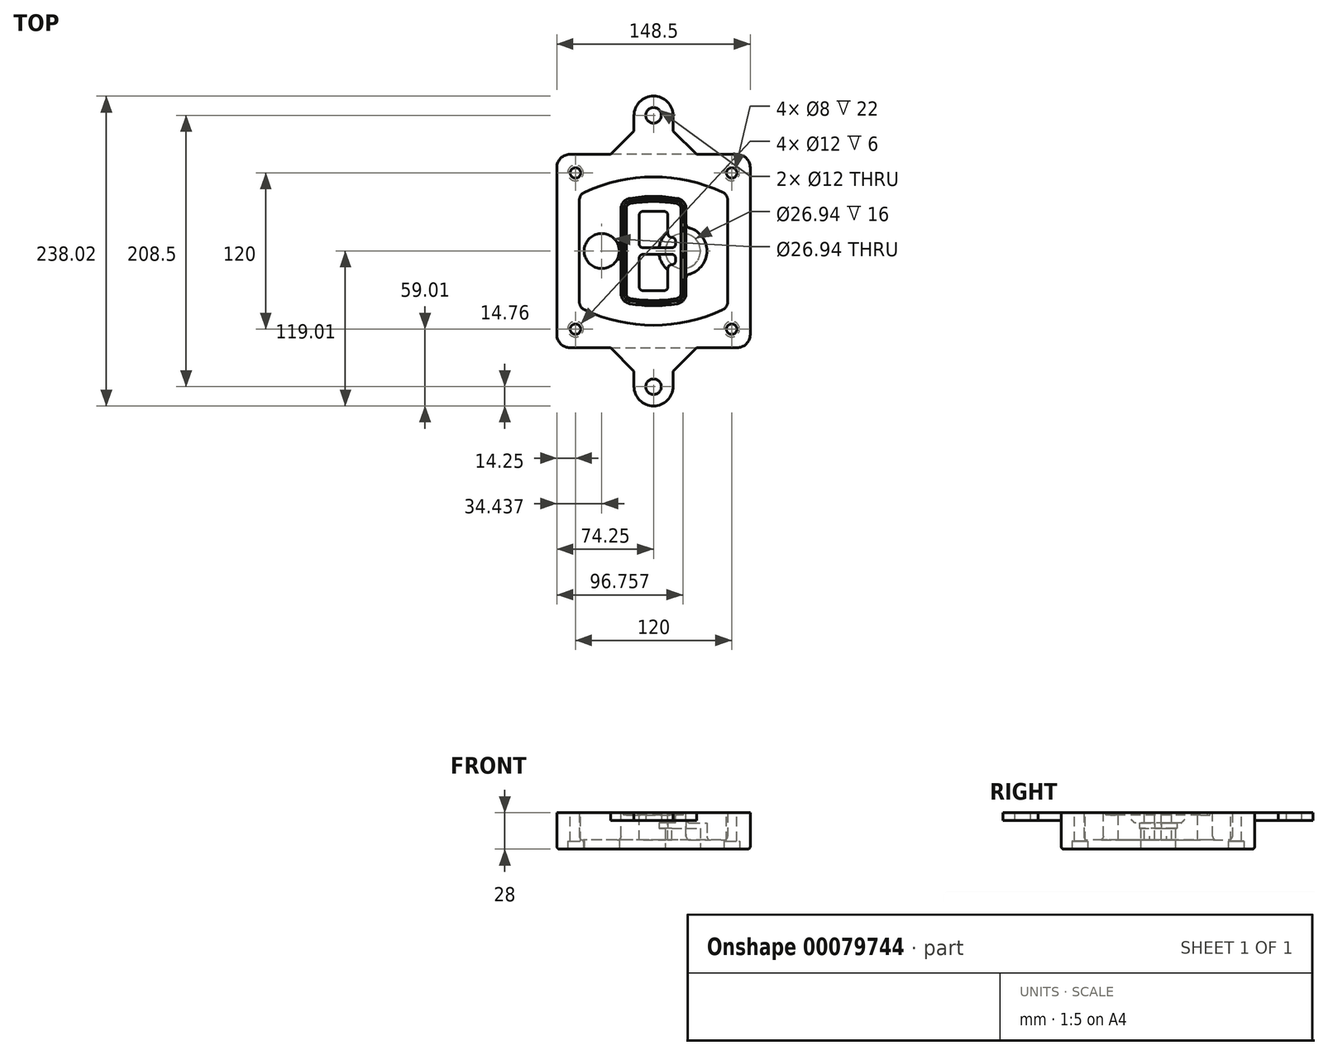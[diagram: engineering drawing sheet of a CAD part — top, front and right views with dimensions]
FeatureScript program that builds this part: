
annotation { "Feature Type Name" : "Feature", "Feature Type Description" : "" }
export const myFeature = defineFeature(function(context is Context, id is Id, definition is map)
    precondition{}
    {
        {
            var Q0;
            Q0=qCreatedBy(makeId("Top.planeOp"),FACE);
            var sketch = newSketch(context, id + "F0", { "sketchPlane" : qUnion([Q0])});
            skPoint(sketch, "E0.rect.middle", {"position": v(0, 0) * mm});
            skLineSegment(sketch, "E1.bottom", {"start": v(-64.25, -74.25) * mm, "end": v(64.25, -74.25) * mm});
            skLineSegment(sketch, "E1.top", {"start": v(-64.25, 74.25) * mm, "end": v(64.25, 74.25) * mm});
            skLineSegment(sketch, "E1.left", {"start": v(-74.25, -64.25) * mm, "end": v(-74.25, 64.25) * mm});
            skLineSegment(sketch, "E1.right", {"start": v(74.25, -64.25) * mm, "end": v(74.25, 64.25) * mm});
            skLineSegment(sketch, "E2", {"start": v(-74.25, 74.25) * mm, "end": v(74.25, -74.25) * mm, "construction": true});
            skLineSegment(sketch, "E3", {"start": v(74.25, 74.25) * mm, "end": v(-74.25, -74.25) * mm, "construction": true});
            skCircle(sketch, "E4", {"center": v(-60, 60) * mm, "radius": 4 * mm});
            skCircle(sketch, "E5", {"center": v(60, 60) * mm, "radius": 4 * mm});
            skCircle(sketch, "E6", {"center": v(60, -60) * mm, "radius": 4 * mm});
            skCircle(sketch, "E7", {"center": v(-60, -60) * mm, "radius": 4 * mm});
            skLineSegment(sketch, "E8", {"start": v(-60, 60) * mm, "end": v(60, 60) * mm, "construction": true});
            skLineSegment(sketch, "E9", {"start": v(60, 60) * mm, "end": v(60, -60) * mm, "construction": true});
            skLineSegment(sketch, "E10", {"start": v(60, -60) * mm, "end": v(-60, -60) * mm, "construction": true});
            skLineSegment(sketch, "E11", {"start": v(-60, -60) * mm, "end": v(-60, 60) * mm, "construction": true});
            skLineSegment(sketch, "E12", {"start": v(-60, 38.83) * mm, "end": v(-60, -38.83) * mm});
            skLineSegment(sketch, "E13", {"start": v(60, 38.83) * mm, "end": v(60, -38.83) * mm});
            skArc(sketch, "E14", {"start": v(54.26, 47.88) * mm, "mid": v(0, 60) * mm, "end": v(-54.26, 47.88) * mm});
            skArc(sketch, "E15", {"start": v(-54.26, -47.88) * mm, "mid": v(0, -60) * mm, "end": v(54.26, -47.88) * mm});
            skLineSegment(sketch, "E16", {"start": v(-60, 0) * mm, "end": v(60, 0) * mm, "construction": true});
            skPoint(sketch, "E17.visualSharp", {"position": v(-60, -45) * mm});
            skArc(sketch, "E17.filletArc", {"start": v(-60, -38.83) * mm, "mid": v(-58.44, -44.2) * mm, "end": v(-54.26, -47.88) * mm});
            skPoint(sketch, "E18.visualSharp", {"position": v(-60, 45) * mm});
            skArc(sketch, "E18.filletArc", {"start": v(-54.26, 47.88) * mm, "mid": v(-58.44, 44.2) * mm, "end": v(-60, 38.83) * mm});
            skPoint(sketch, "E19.visualSharp", {"position": v(60, 45) * mm});
            skArc(sketch, "E19.filletArc", {"start": v(60, 38.83) * mm, "mid": v(58.44, 44.2) * mm, "end": v(54.26, 47.88) * mm});
            skPoint(sketch, "E20.visualSharp", {"position": v(60, -45) * mm});
            skArc(sketch, "E20.filletArc", {"start": v(54.26, -47.88) * mm, "mid": v(58.44, -44.2) * mm, "end": v(60, -38.83) * mm});
            skPoint(sketch, "E21.visualSharp", {"position": v(-74.25, 74.25) * mm});
            skArc(sketch, "E21.filletArc", {"start": v(-64.25, 74.25) * mm, "mid": v(-71.32, 71.32) * mm, "end": v(-74.25, 64.25) * mm});
            skPoint(sketch, "E22.visualSharp", {"position": v(74.25, 74.25) * mm});
            skArc(sketch, "E22.filletArc", {"start": v(74.25, 64.25) * mm, "mid": v(71.32, 71.32) * mm, "end": v(64.25, 74.25) * mm});
            skPoint(sketch, "E23.visualSharp", {"position": v(74.25, -74.25) * mm});
            skArc(sketch, "E23.filletArc", {"start": v(64.25, -74.25) * mm, "mid": v(71.32, -71.32) * mm, "end": v(74.25, -64.25) * mm});
            skPoint(sketch, "E24.visualSharp", {"position": v(-74.25, -74.25) * mm});
            skArc(sketch, "E24.filletArc", {"start": v(-74.25, -64.25) * mm, "mid": v(-71.32, -71.32) * mm, "end": v(-64.25, -74.25) * mm});
            skArc(sketch, "E25.0", {"start": v(57, 38.83) * mm, "mid": v(55.9, 42.58) * mm, "end": v(52.98, 45.17) * mm});
            skLineSegment(sketch, "E25.1", {"start": v(57, 38.83) * mm, "end": v(57, -38.83) * mm});
            skArc(sketch, "E25.2", {"start": v(52.98, -45.17) * mm, "mid": v(55.9, -42.58) * mm, "end": v(57, -38.83) * mm});
            skArc(sketch, "E25.3", {"start": v(-52.98, -45.17) * mm, "mid": v(0, -57) * mm, "end": v(52.98, -45.17) * mm});
            skArc(sketch, "E25.4", {"start": v(-57, -38.83) * mm, "mid": v(-55.9, -42.58) * mm, "end": v(-52.98, -45.17) * mm});
            skArc(sketch, "E25.5", {"start": v(52.98, 45.17) * mm, "mid": v(0, 57) * mm, "end": v(-52.98, 45.17) * mm});
            skLineSegment(sketch, "E25.6", {"start": v(-57, 38.83) * mm, "end": v(-57, -38.83) * mm});
            skArc(sketch, "E25.7", {"start": v(-52.98, 45.17) * mm, "mid": v(-55.9, 42.58) * mm, "end": v(-57, 38.83) * mm});
            skArc(sketch, "E26.0", {"start": v(-55.96, 51.5) * mm, "mid": v(-61.82, 46.33) * mm, "end": v(-64, 38.83) * mm});
            skArc(sketch, "E26.1", {"start": v(55.96, 51.5) * mm, "mid": v(0, 64) * mm, "end": v(-55.96, 51.5) * mm});
            skArc(sketch, "E26.2", {"start": v(64, 38.83) * mm, "mid": v(61.82, 46.33) * mm, "end": v(55.96, 51.5) * mm});
            skLineSegment(sketch, "E26.3", {"start": v(64, 38.83) * mm, "end": v(64, -38.83) * mm});
            skArc(sketch, "E26.4", {"start": v(55.96, -51.5) * mm, "mid": v(61.82, -46.33) * mm, "end": v(64, -38.83) * mm});
            skLineSegment(sketch, "E26.5", {"start": v(-64, 38.83) * mm, "end": v(-64, -38.83) * mm});
            skArc(sketch, "E26.6", {"start": v(-55.96, -51.5) * mm, "mid": v(0, -64) * mm, "end": v(55.96, -51.5) * mm});
            skArc(sketch, "E26.7", {"start": v(-64, -38.83) * mm, "mid": v(-61.82, -46.33) * mm, "end": v(-55.96, -51.5) * mm});
            skSolve(sketch);
        }
        {
            var Q0;
            Q0=makeQuery(id+"F0.imprint","IMPRINT",FACE,{"disambiguationData":[TD([[makeQuery(id+"F0.imprint","IMPRINT",EDGE,{"derivedFrom":sQuery(id+"F0.wireOp",EDGE,"E1.bottom")}),1.0]])]});
            var Q1;
            Q1=makeQuery(id+"F0.imprint","IMPRINT",FACE,{"disambiguationData":[TD([[makeQuery(id+"F0.imprint","IMPRINT",EDGE,{"derivedFrom":sQuery(id+"F0.wireOp",EDGE,"E12")}),1.0]])]});
            var Q2;
            Q2=makeQuery(id+"F0.imprint","IMPRINT",FACE,{"disambiguationData":[TD([[makeQuery(id+"F0.imprint","IMPRINT",EDGE,{"derivedFrom":sQuery(id+"F0.wireOp",EDGE,"E25.0")}),1.0]])]});
            var Q3;
            Q3=makeQuery(id+"F0.imprint","IMPRINT",FACE,{"disambiguationData":[TD([[makeQuery(id+"F0.imprint","IMPRINT",EDGE,{"derivedFrom":sQuery(id+"F0.wireOp",EDGE,"E12")}),-1.0]])]});
            extrude(context, id + "F1", {"entities" : qUnion([Q0, Q1, Q2, Q3]), "oppositeDirection" : true, "depth" : 25 * mm});
        }
        {
            var Q0;
            Q0=makeQuery(id+"F0.imprint","IMPRINT",FACE,{"disambiguationData":[TD([[makeQuery(id+"F0.imprint","IMPRINT",EDGE,{"derivedFrom":sQuery(id+"F0.wireOp",EDGE,"E12")}),1.0]])]});
            extrude(context, id + "F2", {"entities" : qUnion([Q0]), "operationType" : NewBodyOperationType.ADD, "depth" : 3 * mm});
        }
        {
            var Q0;
            Q0=makeQuery(id+"F0.imprint","IMPRINT",FACE,{"disambiguationData":[TD([[makeQuery(id+"F0.imprint","IMPRINT",EDGE,{"derivedFrom":sQuery(id+"F0.wireOp",EDGE,"E25.0")}),1.0]])]});
            extrude(context, id + "F3", {"entities" : qUnion([Q0]), "operationType" : NewBodyOperationType.REMOVE, "oppositeDirection" : true, "depth" : 18 * mm});
        }
        {
            var Q0;
            Q0=makeQuery(id+"F2.opExtrude","CAP_FACE",FACE,{"disambiguationData":[OSD([sQuery(id+"F0.wireOp",EDGE,"E12"),sQuery(id+"F0.wireOp",EDGE,"E13"),sQuery(id+"F0.wireOp",EDGE,"E14"),sQuery(id+"F0.wireOp",EDGE,"E15"),sQuery(id+"F0.wireOp",EDGE,"E17.filletArc"),sQuery(id+"F0.wireOp",EDGE,"E18.filletArc"),sQuery(id+"F0.wireOp",EDGE,"E19.filletArc"),sQuery(id+"F0.wireOp",EDGE,"E20.filletArc"),sQuery(id+"F0.wireOp",EDGE,"E25.0"),sQuery(id+"F0.wireOp",EDGE,"E25.1"),sQuery(id+"F0.wireOp",EDGE,"E25.2"),sQuery(id+"F0.wireOp",EDGE,"E25.3"),sQuery(id+"F0.wireOp",EDGE,"E25.4"),sQuery(id+"F0.wireOp",EDGE,"E25.5"),sQuery(id+"F0.wireOp",EDGE,"E25.6"),sQuery(id+"F0.wireOp",EDGE,"E25.7")])],"isStart":false});
            var sketch = newSketch(context, id + "F4", { "sketchPlane" : qUnion([Q0])});
            skArc(sketch, "E27.0", {"start": v(-18.34, -40.45) * mm, "mid": v(0, -42) * mm, "end": v(18.34, -40.45) * mm});
            skArc(sketch, "E28.0", {"start": v(18.34, 40.45) * mm, "mid": v(0, 42) * mm, "end": v(-18.34, 40.45) * mm});
            skLineSegment(sketch, "E29", {"start": v(-25, 32.57) * mm, "end": v(-25, -32.57) * mm});
            skLineSegment(sketch, "E30", {"start": v(25, 32.57) * mm, "end": v(25, -32.57) * mm});
            skLineSegment(sketch, "E31", {"start": v(-25, 39.1) * mm, "end": v(25, 39.1) * mm, "construction": true});
            skLineSegment(sketch, "E32", {"start": v(-25, -39.1) * mm, "end": v(25, -39.1) * mm, "construction": true});
            skPoint(sketch, "E33.visualSharp", {"position": v(-25, 39.1) * mm});
            skArc(sketch, "E33.filletArc", {"start": v(-18.34, 40.45) * mm, "mid": v(-23.11, 37.73) * mm, "end": v(-25, 32.57) * mm});
            skPoint(sketch, "E34.visualSharp", {"position": v(25, 39.1) * mm});
            skArc(sketch, "E34.filletArc", {"start": v(25, 32.57) * mm, "mid": v(23.11, 37.73) * mm, "end": v(18.34, 40.45) * mm});
            skPoint(sketch, "E35.visualSharp", {"position": v(25, -39.1) * mm});
            skArc(sketch, "E35.filletArc", {"start": v(18.34, -40.45) * mm, "mid": v(23.11, -37.73) * mm, "end": v(25, -32.57) * mm});
            skPoint(sketch, "E36.visualSharp", {"position": v(-25, -39.1) * mm});
            skArc(sketch, "E36.filletArc", {"start": v(-25, -32.57) * mm, "mid": v(-23.11, -37.73) * mm, "end": v(-18.34, -40.45) * mm});
            skArc(sketch, "E37.0", {"start": v(52.98, 45.17) * mm, "mid": v(0, 57) * mm, "end": v(-52.98, 45.17) * mm});
            skArc(sketch, "E37.1", {"start": v(-52.98, 45.17) * mm, "mid": v(-55.9, 42.58) * mm, "end": v(-57, 38.83) * mm});
            skLineSegment(sketch, "E37.2", {"start": v(-57, 38.83) * mm, "end": v(-57, -38.83) * mm});
            skArc(sketch, "E37.3", {"start": v(-57, -38.83) * mm, "mid": v(-55.9, -42.58) * mm, "end": v(-52.98, -45.17) * mm});
            skArc(sketch, "E37.4", {"start": v(-52.98, -45.17) * mm, "mid": v(0, -57) * mm, "end": v(52.98, -45.17) * mm});
            skArc(sketch, "E37.5", {"start": v(52.98, -45.17) * mm, "mid": v(55.9, -42.58) * mm, "end": v(57, -38.83) * mm});
            skLineSegment(sketch, "E37.6", {"start": v(57, 38.83) * mm, "end": v(57, -38.83) * mm});
            skArc(sketch, "E37.7", {"start": v(57, 38.83) * mm, "mid": v(55.9, 42.58) * mm, "end": v(52.98, 45.17) * mm});
            skLineSegment(sketch, "E38.0", {"start": v(23, 32.57) * mm, "end": v(23, -32.57) * mm});
            skArc(sketch, "E38.1", {"start": v(18, -38.48) * mm, "mid": v(21.58, -36.44) * mm, "end": v(23, -32.57) * mm});
            skArc(sketch, "E38.2", {"start": v(-18, -38.48) * mm, "mid": v(0, -40) * mm, "end": v(18, -38.48) * mm});
            skArc(sketch, "E38.3", {"start": v(-23, -32.57) * mm, "mid": v(-21.58, -36.44) * mm, "end": v(-18, -38.48) * mm});
            skLineSegment(sketch, "E38.4", {"start": v(-23, 32.57) * mm, "end": v(-23, -32.57) * mm});
            skArc(sketch, "E38.5", {"start": v(23, 32.57) * mm, "mid": v(21.58, 36.44) * mm, "end": v(18, 38.48) * mm});
            skArc(sketch, "E38.6", {"start": v(-18, 38.48) * mm, "mid": v(-21.58, 36.44) * mm, "end": v(-23, 32.57) * mm});
            skArc(sketch, "E38.7", {"start": v(18, 38.48) * mm, "mid": v(0, 40) * mm, "end": v(-18, 38.48) * mm});
            skArc(sketch, "E39.0", {"start": v(21, 32.57) * mm, "mid": v(20.06, 35.15) * mm, "end": v(17.67, 36.5) * mm});
            skLineSegment(sketch, "E39.1", {"start": v(21, 32.57) * mm, "end": v(21, -32.57) * mm});
            skArc(sketch, "E39.2", {"start": v(17.67, -36.5) * mm, "mid": v(20.06, -35.15) * mm, "end": v(21, -32.57) * mm});
            skArc(sketch, "E39.3", {"start": v(-17.67, -36.5) * mm, "mid": v(0, -38) * mm, "end": v(17.67, -36.5) * mm});
            skArc(sketch, "E39.4", {"start": v(-21, -32.57) * mm, "mid": v(-20.06, -35.15) * mm, "end": v(-17.67, -36.5) * mm});
            skArc(sketch, "E39.5", {"start": v(17.67, 36.5) * mm, "mid": v(0, 38) * mm, "end": v(-17.67, 36.5) * mm});
            skLineSegment(sketch, "E39.6", {"start": v(-21, 32.57) * mm, "end": v(-21, -32.57) * mm});
            skArc(sketch, "E39.7", {"start": v(-17.67, 36.5) * mm, "mid": v(-20.06, 35.15) * mm, "end": v(-21, 32.57) * mm});
            skLineSegment(sketch, "E40", {"start": v(-25, 0) * mm, "end": v(25, 0) * mm, "construction": true});
            skLineSegment(sketch, "E41", {"start": v(-11, 5.5) * mm, "end": v(-11, 27.5) * mm});
            skLineSegment(sketch, "E42", {"start": v(-8, 30.5) * mm, "end": v(8, 30.5) * mm});
            skLineSegment(sketch, "E43", {"start": v(11, 27.5) * mm, "end": v(11, 13.5) * mm});
            skLineSegment(sketch, "E44", {"start": v(14, 10.5) * mm, "end": v(14, 10.5) * mm});
            skLineSegment(sketch, "E45", {"start": v(17, 7.5) * mm, "end": v(17, 5.5) * mm});
            skLineSegment(sketch, "E46", {"start": v(14, 2.5) * mm, "end": v(-8, 2.5) * mm});
            skPoint(sketch, "E47.visualSharp", {"position": v(-11, 30.5) * mm});
            skArc(sketch, "E47.filletArc", {"start": v(-8, 30.5) * mm, "mid": v(-10.12, 29.62) * mm, "end": v(-11, 27.5) * mm});
            skPoint(sketch, "E48.visualSharp", {"position": v(11, 30.5) * mm});
            skArc(sketch, "E48.filletArc", {"start": v(11, 27.5) * mm, "mid": v(10.12, 29.62) * mm, "end": v(8, 30.5) * mm});
            skPoint(sketch, "E49.visualSharp", {"position": v(11, 10.5) * mm});
            skArc(sketch, "E49.filletArc", {"start": v(11, 13.5) * mm, "mid": v(11.88, 11.38) * mm, "end": v(14, 10.5) * mm});
            skPoint(sketch, "E50.visualSharp", {"position": v(17, 10.5) * mm});
            skArc(sketch, "E50.filletArc", {"start": v(17, 7.5) * mm, "mid": v(16.12, 9.62) * mm, "end": v(14, 10.5) * mm});
            skPoint(sketch, "E51.visualSharp", {"position": v(17, 2.5) * mm});
            skArc(sketch, "E51.filletArc", {"start": v(14, 2.5) * mm, "mid": v(16.12, 3.38) * mm, "end": v(17, 5.5) * mm});
            skPoint(sketch, "E52.visualSharp", {"position": v(-11, 2.5) * mm});
            skArc(sketch, "E52.filletArc", {"start": v(-11, 5.5) * mm, "mid": v(-10.12, 3.38) * mm, "end": v(-8, 2.5) * mm});
            skLineSegment(sketch, "E53.0.MirrorCS", {"start": v(14, -2.5) * mm, "end": v(-8, -2.5) * mm});
            skArc(sketch, "E54.0.MirrorCS", {"start": v(-11, -5.5) * mm, "mid": v(-10.12, -3.38) * mm, "end": v(-8, -2.5) * mm});
            skLineSegment(sketch, "E55.0.MirrorCS", {"start": v(-11, -5.5) * mm, "end": v(-11, -27.5) * mm});
            skArc(sketch, "E56.0.MirrorCS", {"start": v(-8, -30.5) * mm, "mid": v(-10.12, -29.62) * mm, "end": v(-11, -27.5) * mm});
            skLineSegment(sketch, "E57.0.MirrorCS", {"start": v(-8, -30.5) * mm, "end": v(8, -30.5) * mm});
            skArc(sketch, "E58.0.MirrorCS", {"start": v(11, -27.5) * mm, "mid": v(10.12, -29.62) * mm, "end": v(8, -30.5) * mm});
            skLineSegment(sketch, "E59.0.MirrorCS", {"start": v(11, -27.5) * mm, "end": v(11, -13.5) * mm});
            skArc(sketch, "E60.0.MirrorCS", {"start": v(11, -13.5) * mm, "mid": v(11.88, -11.38) * mm, "end": v(14, -10.5) * mm});
            skArc(sketch, "E61.0.MirrorCS", {"start": v(17, -7.5) * mm, "mid": v(16.12, -9.62) * mm, "end": v(14, -10.5) * mm});
            skLineSegment(sketch, "E62.0.MirrorCS", {"start": v(17, -7.5) * mm, "end": v(17, -5.5) * mm});
            skArc(sketch, "E63.0.MirrorCS", {"start": v(14, -2.5) * mm, "mid": v(16.12, -3.38) * mm, "end": v(17, -5.5) * mm});
            skSolve(sketch);
        }
        {
            var Q0;
            Q0=makeQuery(id+"F4.imprint","IMPRINT",FACE,{"disambiguationData":[TD([[makeQuery(id+"F4.imprint","IMPRINT",EDGE,{"derivedFrom":sQuery(id+"F4.wireOp",EDGE,"E27.0")}),1.0]])]});
            var Q1;
            Q1=makeQuery(id+"F4.imprint","IMPRINT",FACE,{"disambiguationData":[TD([[makeQuery(id+"F4.imprint","IMPRINT",EDGE,{"derivedFrom":sQuery(id+"F4.wireOp",EDGE,"E38.0")}),-1.0]])]});
            var Q2;
            Q2=makeQuery(id+"F4.imprint","IMPRINT",FACE,{"disambiguationData":[TD([[makeQuery(id+"F4.imprint","IMPRINT",EDGE,{"derivedFrom":sQuery(id+"F4.wireOp",EDGE,"E39.0")}),1.0]])]});
            extrude(context, id + "F5", {"entities" : qUnion([Q0, Q1, Q2]), "operationType" : NewBodyOperationType.ADD, "endBound" : BoundingType.UP_TO_NEXT, "oppositeDirection" : true, "depth" : 25 * mm});
        }
        {
            var Q0;
            Q0=makeQuery(id+"F4.imprint","IMPRINT",FACE,{"disambiguationData":[TD([[makeQuery(id+"F4.imprint","IMPRINT",EDGE,{"derivedFrom":sQuery(id+"F4.wireOp",EDGE,"E38.0")}),-1.0]])]});
            extrude(context, id + "F6", {"entities" : qUnion([Q0]), "operationType" : NewBodyOperationType.REMOVE, "oppositeDirection" : true, "depth" : 2 * mm});
        }
        {
            var Q0;
            Q0=makeQuery(id+"F1.opExtrude","CAP_FACE",FACE,{"disambiguationData":[OSD([sQuery(id+"F0.wireOp",EDGE,"E1.bottom"),sQuery(id+"F0.wireOp",EDGE,"E1.top"),sQuery(id+"F0.wireOp",EDGE,"E1.left"),sQuery(id+"F0.wireOp",EDGE,"E1.right"),sQuery(id+"F0.wireOp",EDGE,"E4"),sQuery(id+"F0.wireOp",EDGE,"E5"),sQuery(id+"F0.wireOp",EDGE,"E6"),sQuery(id+"F0.wireOp",EDGE,"E7"),sQuery(id+"F0.wireOp",EDGE,"E21.filletArc"),sQuery(id+"F0.wireOp",EDGE,"E22.filletArc"),sQuery(id+"F0.wireOp",EDGE,"E23.filletArc"),sQuery(id+"F0.wireOp",EDGE,"E24.filletArc")])],"isStart":false});
            var sketch = newSketch(context, id + "F7", { "sketchPlane" : qUnion([Q0])});
            skCircle(sketch, "E64", {"center": v(22.5, 0) * mm, "radius": 13.47 * mm});
            skCircle(sketch, "E65", {"center": v(-39.81, 0) * mm, "radius": 13.47 * mm});
            skLineSegment(sketch, "E66", {"start": v(74.25, 0) * mm, "end": v(-74.25, 0) * mm});
            skCircle(sketch, "E67", {"center": v(22.5, 0) * mm, "radius": 18.47 * mm});
            skCircle(sketch, "E68", {"center": v(60, -60) * mm, "radius": 6 * mm});
            skCircle(sketch, "E69", {"center": v(-60, -60) * mm, "radius": 6 * mm});
            skCircle(sketch, "E70", {"center": v(-60, 60) * mm, "radius": 6 * mm});
            skCircle(sketch, "E71", {"center": v(60, 60) * mm, "radius": 6 * mm});
            skSolve(sketch);
        }
        {
            var Q0;
            {var subQ1=sQuery(id+"F7.wireOp",EDGE,"E66");var subQ4=sQuery(id+"F7.wireOp",EDGE,"E64");var subQ6=makeQuery(id+"F7.imprint","INTERSECT",VERTEX,{"disambiguationData":[OD(0.0)],"derivedFrom":[subQ4,subQ1]});Q0=makeQuery(id+"F7.imprint","IMPRINT",FACE,{"disambiguationData":[TD([[makeQuery(id+"F7.imprint","IMPRINT",EDGE,{"disambiguationData":[TD([[subQ6,-1.0]])],"derivedFrom":subQ4}),-1.0]])]});}
            var Q1;
            {var subQ0=sQuery(id+"F7.wireOp",EDGE,"E66");var subQ1=sQuery(id+"F7.wireOp",EDGE,"E64");var subQ3=makeQuery(id+"F7.imprint","INTERSECT",VERTEX,{"disambiguationData":[OD(0.0)],"derivedFrom":[subQ1,subQ0]});Q1=makeQuery(id+"F7.imprint","IMPRINT",FACE,{"disambiguationData":[TD([[makeQuery(id+"F7.imprint","IMPRINT",EDGE,{"disambiguationData":[TD([[subQ3,-1.0]])],"derivedFrom":subQ1}),1.0]])]});}
            var Q2;
            {var subQ0=sQuery(id+"F7.wireOp",EDGE,"E66");var subQ1=sQuery(id+"F7.wireOp",EDGE,"E64");var subQ3=makeQuery(id+"F7.imprint","INTERSECT",VERTEX,{"disambiguationData":[OD(0.0)],"derivedFrom":[subQ1,subQ0]});Q2=makeQuery(id+"F7.imprint","IMPRINT",FACE,{"disambiguationData":[TD([[makeQuery(id+"F7.imprint","IMPRINT",EDGE,{"disambiguationData":[TD([[subQ3,1.0]])],"derivedFrom":subQ1}),1.0]])]});}
            var Q3;
            {var subQ1=sQuery(id+"F7.wireOp",EDGE,"E66");var subQ4=sQuery(id+"F7.wireOp",EDGE,"E64");var subQ6=makeQuery(id+"F7.imprint","INTERSECT",VERTEX,{"disambiguationData":[OD(0.0)],"derivedFrom":[subQ4,subQ1]});Q3=makeQuery(id+"F7.imprint","IMPRINT",FACE,{"disambiguationData":[TD([[makeQuery(id+"F7.imprint","IMPRINT",EDGE,{"disambiguationData":[TD([[subQ6,1.0]])],"derivedFrom":subQ4}),-1.0]])]});}
            extrude(context, id + "F8", {"entities" : qUnion([Q0, Q1, Q2, Q3]), "operationType" : NewBodyOperationType.ADD, "oppositeDirection" : true, "depth" : 20 * mm});
        }
        {
            var Q0;
            {var subQ0=sQuery(id+"F7.wireOp",EDGE,"E66");var subQ1=sQuery(id+"F7.wireOp",EDGE,"E64");var subQ3=makeQuery(id+"F7.imprint","INTERSECT",VERTEX,{"disambiguationData":[OD(0.0)],"derivedFrom":[subQ1,subQ0]});Q0=makeQuery(id+"F7.imprint","IMPRINT",FACE,{"disambiguationData":[TD([[makeQuery(id+"F7.imprint","IMPRINT",EDGE,{"disambiguationData":[TD([[subQ3,-1.0]])],"derivedFrom":subQ1}),1.0]])]});}
            var Q1;
            {var subQ0=sQuery(id+"F7.wireOp",EDGE,"E66");var subQ1=sQuery(id+"F7.wireOp",EDGE,"E64");var subQ3=makeQuery(id+"F7.imprint","INTERSECT",VERTEX,{"disambiguationData":[OD(0.0)],"derivedFrom":[subQ1,subQ0]});Q1=makeQuery(id+"F7.imprint","IMPRINT",FACE,{"disambiguationData":[TD([[makeQuery(id+"F7.imprint","IMPRINT",EDGE,{"disambiguationData":[TD([[subQ3,1.0]])],"derivedFrom":subQ1}),1.0]])]});}
            extrude(context, id + "F9", {"entities" : qUnion([Q0, Q1]), "operationType" : NewBodyOperationType.REMOVE, "oppositeDirection" : true, "depth" : 16 * mm});
        }
        {
            var Q0;
            {var subQ0=sQuery(id+"F7.wireOp",EDGE,"E66");var subQ1=sQuery(id+"F7.wireOp",EDGE,"E65");var subQ3=makeQuery(id+"F7.imprint","INTERSECT",VERTEX,{"disambiguationData":[OD(0.0)],"derivedFrom":[subQ1,subQ0]});Q0=makeQuery(id+"F7.imprint","IMPRINT",FACE,{"disambiguationData":[TD([[makeQuery(id+"F7.imprint","IMPRINT",EDGE,{"disambiguationData":[TD([[subQ3,-1.0]])],"derivedFrom":subQ1}),1.0]])]});}
            var Q1;
            {var subQ0=sQuery(id+"F7.wireOp",EDGE,"E66");var subQ1=sQuery(id+"F7.wireOp",EDGE,"E65");var subQ3=makeQuery(id+"F7.imprint","INTERSECT",VERTEX,{"disambiguationData":[OD(0.0)],"derivedFrom":[subQ1,subQ0]});Q1=makeQuery(id+"F7.imprint","IMPRINT",FACE,{"disambiguationData":[TD([[makeQuery(id+"F7.imprint","IMPRINT",EDGE,{"disambiguationData":[TD([[subQ3,1.0]])],"derivedFrom":subQ1}),1.0]])]});}
            extrude(context, id + "F10", {"entities" : qUnion([Q0, Q1]), "operationType" : NewBodyOperationType.REMOVE, "oppositeDirection" : true, "depth" : 25 * mm});
        }
        {
            var Q0;
            Q0=makeQuery(id+"F7.imprint","IMPRINT",FACE,{"disambiguationData":[TD([[makeQuery(id+"F7.imprint","IMPRINT",EDGE,{"derivedFrom":sQuery(id+"F7.wireOp",EDGE,"E68")}),1.0]])]});
            var Q1;
            Q1=makeQuery(id+"F7.imprint","IMPRINT",FACE,{"disambiguationData":[TD([[makeQuery(id+"F7.imprint","IMPRINT",EDGE,{"derivedFrom":makeQuery(id+"F1.opExtrude","CAP_EDGE",EDGE,{"disambiguationData":[OSD([sQuery(id+"F0.wireOp",EDGE,"E5")])],"isStart":false})}),-1.0]])]});
            var Q2;
            Q2=makeQuery(id+"F7.imprint","IMPRINT",FACE,{"disambiguationData":[TD([[makeQuery(id+"F7.imprint","IMPRINT",EDGE,{"derivedFrom":sQuery(id+"F7.wireOp",EDGE,"E69")}),1.0]])]});
            var Q3;
            Q3=makeQuery(id+"F7.imprint","IMPRINT",FACE,{"disambiguationData":[TD([[makeQuery(id+"F7.imprint","IMPRINT",EDGE,{"derivedFrom":makeQuery(id+"F1.opExtrude","CAP_EDGE",EDGE,{"disambiguationData":[OSD([sQuery(id+"F0.wireOp",EDGE,"E4")])],"isStart":false})}),-1.0]])]});
            var Q4;
            Q4=makeQuery(id+"F7.imprint","IMPRINT",FACE,{"disambiguationData":[TD([[makeQuery(id+"F7.imprint","IMPRINT",EDGE,{"derivedFrom":sQuery(id+"F7.wireOp",EDGE,"E70")}),1.0]])]});
            var Q5;
            Q5=makeQuery(id+"F7.imprint","IMPRINT",FACE,{"disambiguationData":[TD([[makeQuery(id+"F7.imprint","IMPRINT",EDGE,{"derivedFrom":makeQuery(id+"F1.opExtrude","CAP_EDGE",EDGE,{"disambiguationData":[OSD([sQuery(id+"F0.wireOp",EDGE,"E7")])],"isStart":false})}),-1.0]])]});
            var Q6;
            Q6=makeQuery(id+"F7.imprint","IMPRINT",FACE,{"disambiguationData":[TD([[makeQuery(id+"F7.imprint","IMPRINT",EDGE,{"derivedFrom":sQuery(id+"F7.wireOp",EDGE,"E71")}),1.0]])]});
            var Q7;
            Q7=makeQuery(id+"F7.imprint","IMPRINT",FACE,{"disambiguationData":[TD([[makeQuery(id+"F7.imprint","IMPRINT",EDGE,{"derivedFrom":makeQuery(id+"F1.opExtrude","CAP_EDGE",EDGE,{"disambiguationData":[OSD([sQuery(id+"F0.wireOp",EDGE,"E6")])],"isStart":false})}),-1.0]])]});
            extrude(context, id + "F11", {"entities" : qUnion([Q0, Q1, Q2, Q3, Q4, Q5, Q6, Q7]), "operationType" : NewBodyOperationType.REMOVE, "oppositeDirection" : true, "depth" : 6 * mm});
        }
        {
            var Q0;
            Q0=makeQuery(id+"F9.boolean.opBoolean","COPY",FACE,{"derivedFrom":makeQuery(id+"F9.opExtrude","CAP_FACE",FACE,{"disambiguationData":[OSD([sQuery(id+"F7.wireOp",EDGE,"E64")])],"isStart":false})});
            var sketch = newSketch(context, id + "F12", { "sketchPlane" : qUnion([Q0])});
            skArc(sketch, "E72.0", {"start": v(11, 14.45) * mm, "mid": v(6.45, 9.13) * mm, "end": v(4.2, 2.5) * mm});
            skArc(sketch, "E72.1", {"start": v(4.2, -2.5) * mm, "mid": v(6.45, -9.13) * mm, "end": v(11, -14.45) * mm});
            skLineSegment(sketch, "E73", {"start": v(4.2, -2.5) * mm, "end": v(14, -2.5) * mm});
            skLineSegment(sketch, "E74.0", {"start": v(14, 2.5) * mm, "end": v(4.2, 2.5) * mm});
            skArc(sketch, "E74.1", {"start": v(14, 2.5) * mm, "mid": v(16.12, 3.38) * mm, "end": v(17, 5.5) * mm});
            skLineSegment(sketch, "E74.2", {"start": v(17, 7.5) * mm, "end": v(17, 5.5) * mm});
            skArc(sketch, "E74.3", {"start": v(17, 7.5) * mm, "mid": v(16.12, 9.62) * mm, "end": v(14, 10.5) * mm});
            skArc(sketch, "E74.4", {"start": v(11, 13.5) * mm, "mid": v(11.88, 11.38) * mm, "end": v(14, 10.5) * mm});
            skLineSegment(sketch, "E74.5", {"start": v(11, 14.45) * mm, "end": v(11, 13.5) * mm});
            skLineSegment(sketch, "E74.7", {"start": v(14, -2.5) * mm, "end": v(4.2, -2.5) * mm});
            skArc(sketch, "E74.8", {"start": v(14, -2.5) * mm, "mid": v(16.12, -3.38) * mm, "end": v(17, -5.5) * mm});
            skLineSegment(sketch, "E74.9", {"start": v(17, -7.5) * mm, "end": v(17, -5.5) * mm});
            skArc(sketch, "E74.10", {"start": v(17, -7.5) * mm, "mid": v(16.12, -9.62) * mm, "end": v(14, -10.5) * mm});
            skArc(sketch, "E74.11", {"start": v(11, -13.5) * mm, "mid": v(11.88, -11.38) * mm, "end": v(14, -10.5) * mm});
            skLineSegment(sketch, "E74.12", {"start": v(11, -14.45) * mm, "end": v(11, -13.5) * mm});
            skPoint(sketch, "E75.orphan", {"position": v(11, -27.5) * mm});
            skPoint(sketch, "E76.orphan", {"position": v(-8, -2.5) * mm});
            skPoint(sketch, "E77.orphan", {"position": v(-8, 2.5) * mm});
            skPoint(sketch, "E78.orphan", {"position": v(11, 27.5) * mm});
            skSolve(sketch);
        }
        {
            var Q0;
            {var subQ7=sQuery(id+"F12.wireOp",EDGE,"E72.0");var subQ14=sQuery(id+"F12.wireOp",EDGE,"E72.1");var subQ16=sQuery(id+"F12.wireOp",EDGE,"E74.1");var subQ18=sQuery(id+"F12.wireOp",EDGE,"E74.8");Q0=qUnion([makeQuery(id+"F12.imprint","IMPRINT",FACE,{"disambiguationData":[TD([[makeQuery(id+"F12.imprint","IMPRINT",EDGE,{"derivedFrom":subQ7}),1.0]])]}),makeQuery(id+"F12.imprint","IMPRINT",FACE,{"disambiguationData":[TD([[makeQuery(id+"F12.imprint","IMPRINT",EDGE,{"derivedFrom":subQ14}),1.0]])]}),makeQuery(id+"F12.imprint","IMPRINT",FACE,{"disambiguationData":[TD([[makeQuery(id+"F12.imprint","IMPRINT",EDGE,{"derivedFrom":subQ16}),1.0]])]}),makeQuery(id+"F12.imprint","IMPRINT",FACE,{"disambiguationData":[TD([[makeQuery(id+"F12.imprint","IMPRINT",EDGE,{"derivedFrom":subQ18}),-1.0]])]})]);}
            var Q1;
            Q1=makeQuery(id+"F5.boolean.opBoolean","SPLIT",FACE,{"disambiguationData":[TD([makeQuery(id+"F5.opExtrude","SWEPT_FACE",FACE,{"disambiguationData":[OSD([sQuery(id+"F4.wireOp",EDGE,"E41")])]})])],"derivedFrom":makeQuery(id+"F3.boolean.opBoolean","COPY",FACE,{"derivedFrom":makeQuery(id+"F3.opExtrude","CAP_FACE",FACE,{"disambiguationData":[OSD([sQuery(id+"F0.wireOp",EDGE,"E25.0"),sQuery(id+"F0.wireOp",EDGE,"E25.1"),sQuery(id+"F0.wireOp",EDGE,"E25.2"),sQuery(id+"F0.wireOp",EDGE,"E25.3"),sQuery(id+"F0.wireOp",EDGE,"E25.4"),sQuery(id+"F0.wireOp",EDGE,"E25.5"),sQuery(id+"F0.wireOp",EDGE,"E25.6"),sQuery(id+"F0.wireOp",EDGE,"E25.7")])],"isStart":false})})});
            extrude(context, id + "F13", {"entities" : qUnion([Q0]), "operationType" : NewBodyOperationType.REMOVE, "endBound" : BoundingType.UP_TO_SURFACE, "endBoundEntityFace" : qUnion([Q1]), "depth" : 25 * mm});
        }
        {
            var Q0;
            Q0=makeQuery(id+"F3.boolean.opBoolean","COPY",EDGE,{"derivedFrom":makeQuery(id+"F3.opExtrude","CAP_EDGE",EDGE,{"disambiguationData":[OSD([sQuery(id+"F0.wireOp",EDGE,"E25.6")])],"isStart":false})});
            var Q1;
            Q1=makeQuery(id+"F8.boolean.opBoolean","INTERSECT",EDGE,{"derivedFrom":[makeQuery(id+"F5.opExtrude","SWEPT_FACE",FACE,{"disambiguationData":[OSD([sQuery(id+"F4.wireOp",EDGE,"E30")])]}),makeQuery(id+"F8.opExtrude","CAP_FACE",FACE,{"disambiguationData":[OSD([sQuery(id+"F7.wireOp",EDGE,"E67")])],"isStart":false})]});
            var Q2;
            Q2=makeQuery(id+"F8.boolean.opBoolean","INTERSECT",EDGE,{"disambiguationData":[OD(1.0)],"derivedFrom":[makeQuery(id+"F5.opExtrude","SWEPT_FACE",FACE,{"disambiguationData":[OSD([sQuery(id+"F4.wireOp",EDGE,"E30")])]}),makeQuery(id+"F8.opExtrude","SWEPT_FACE",FACE,{"disambiguationData":[OSD([sQuery(id+"F7.wireOp",EDGE,"E67")])]})]});
            var Q3;
            {var subQ0=sQuery(id+"F4.wireOp",EDGE,"E30");Q3=makeQuery(id+"F8.boolean.opBoolean","SPLIT",EDGE,{"disambiguationData":[TD([makeQuery(id+"F5.opExtrude","SWEPT_FACE",FACE,{"disambiguationData":[OSD([sQuery(id+"F4.wireOp",EDGE,"E35.filletArc")])]})])],"derivedFrom":makeQuery(id+"F5.opExtrude","CAP_EDGE",EDGE,{"disambiguationData":[OSD([subQ0])],"isStart":false})});}
            var Q4;
            {var subQ0=sQuery(id+"F0.wireOp",EDGE,"E25.7");var subQ1=sQuery(id+"F0.wireOp",EDGE,"E25.1");var subQ2=sQuery(id+"F0.wireOp",EDGE,"E25.6");var subQ3=sQuery(id+"F0.wireOp",EDGE,"E25.5");var subQ4=sQuery(id+"F0.wireOp",EDGE,"E25.4");var subQ5=sQuery(id+"F0.wireOp",EDGE,"E25.0");var subQ6=sQuery(id+"F0.wireOp",EDGE,"E25.2");var subQ7=sQuery(id+"F0.wireOp",EDGE,"E25.3");Q4=makeQuery(id+"F8.boolean.opBoolean","INTERSECT",EDGE,{"derivedFrom":[makeQuery(id+"F5.boolean.opBoolean","SPLIT",FACE,{"disambiguationData":[TD([makeQuery(id+"F2.opExtrude","SWEPT_FACE",FACE,{"disambiguationData":[OSD([subQ5])]})])],"derivedFrom":makeQuery(id+"F3.boolean.opBoolean","COPY",FACE,{"derivedFrom":makeQuery(id+"F3.opExtrude","CAP_FACE",FACE,{"disambiguationData":[OSD([subQ5,subQ1,subQ6,subQ7,subQ4,subQ3,subQ2,subQ0])],"isStart":false})})}),makeQuery(id+"F8.opExtrude","SWEPT_FACE",FACE,{"disambiguationData":[OSD([sQuery(id+"F7.wireOp",EDGE,"E67")])]})]});}
            var Q5;
            Q5=makeQuery(id+"F8.boolean.opBoolean","INTERSECT",EDGE,{"disambiguationData":[OD(0.0)],"derivedFrom":[makeQuery(id+"F5.opExtrude","SWEPT_FACE",FACE,{"disambiguationData":[OSD([sQuery(id+"F4.wireOp",EDGE,"E30")])]}),makeQuery(id+"F8.opExtrude","SWEPT_FACE",FACE,{"disambiguationData":[OSD([sQuery(id+"F7.wireOp",EDGE,"E67")])]})]});
            fillet(context, id + "F14", {"entities" : qUnion([Q0, Q1, Q2, Q3, Q4, Q5]), "radius" : 3 * mm, "tangentPropagation" : true, "allowEdgeOverflow" : false});
        }
        {
            var Q0;
            Q0=makeQuery(id+"F1.opExtrude","CAP_EDGE",EDGE,{"disambiguationData":[OSD([sQuery(id+"F0.wireOp",EDGE,"E1.bottom")])],"isStart":false});
            fillet(context, id + "F15", {"entities" : qUnion([Q0]), "radius" : 2 * mm, "tangentPropagation" : true, "allowEdgeOverflow" : false});
        }
        {
            var Q0;
            {var subQ0=sQuery(id+"F0.wireOp",EDGE,"E22.filletArc");var subQ1=sQuery(id+"F0.wireOp",EDGE,"E7");var subQ2=sQuery(id+"F0.wireOp",EDGE,"E6");var subQ3=sQuery(id+"F0.wireOp",EDGE,"E5");var subQ4=sQuery(id+"F0.wireOp",EDGE,"E4");var subQ5=sQuery(id+"F0.wireOp",EDGE,"E1.bottom");var subQ6=sQuery(id+"F0.wireOp",EDGE,"E21.filletArc");var subQ7=sQuery(id+"F0.wireOp",EDGE,"E1.top");var subQ8=sQuery(id+"F0.wireOp",EDGE,"E1.left");var subQ9=sQuery(id+"F0.wireOp",EDGE,"E1.right");var subQ10=sQuery(id+"F0.wireOp",EDGE,"E23.filletArc");var subQ11=sQuery(id+"F0.wireOp",EDGE,"E24.filletArc");Q0=makeQuery(id+"F2.boolean.opBoolean","SPLIT",FACE,{"disambiguationData":[TD([makeQuery(id+"F1.opExtrude","SWEPT_FACE",FACE,{"disambiguationData":[OSD([subQ5])]})])],"derivedFrom":makeQuery(id+"F1.opExtrude","CAP_FACE",FACE,{"disambiguationData":[OSD([subQ5,subQ7,subQ8,subQ9,subQ4,subQ3,subQ2,subQ1,subQ6,subQ0,subQ10,subQ11])],"isStart":true})});}
            var sketch = newSketch(context, id + "F16", { "sketchPlane" : qUnion([Q0])});
            skCircle(sketch, "E79", {"center": v(0, 104.25) * mm, "radius": 6 * mm});
            skLineSegment(sketch, "E80", {"start": v(0, 104.25) * mm, "end": v(0, 74.25) * mm, "construction": true});
            skLineSegment(sketch, "E81", {"start": v(-15, 104) * mm, "end": v(-15, 92.25) * mm});
            skLineSegment(sketch, "E82.MirrorCS", {"start": v(15, 104) * mm, "end": v(15, 92.25) * mm});
            skLineSegment(sketch, "E83", {"start": v(-15, 92.25) * mm, "end": v(-33, 74.25) * mm});
            skLineSegment(sketch, "E84.MirrorCS", {"start": v(15, 92.25) * mm, "end": v(33, 74.25) * mm});
            skLineSegment(sketch, "E85", {"start": v(-74.25, 0) * mm, "end": v(74.25, 0) * mm, "construction": true});
            skArc(sketch, "E86", {"start": v(15, 104) * mm, "mid": v(0, 119) * mm, "end": v(-15, 104) * mm});
            skLineSegment(sketch, "E87.MirrorCS", {"start": v(15, -104) * mm, "end": v(15, -92.25) * mm});
            skLineSegment(sketch, "E88.MirrorCS", {"start": v(-15, -104) * mm, "end": v(-15, -92.25) * mm});
            skCircle(sketch, "E89.MirrorC", {"center": v(0, -104.25) * mm, "radius": 6 * mm});
            skLineSegment(sketch, "E90", {"start": v(15, -92.25) * mm, "end": v(33, -74.25) * mm});
            skLineSegment(sketch, "E91", {"start": v(-15, -92.25) * mm, "end": v(-33, -74.25) * mm});
            skArc(sketch, "E92", {"start": v(-15, -104) * mm, "mid": v(0, -119) * mm, "end": v(15, -104) * mm});
            skArc(sketch, "E93.0", {"start": v(-64.25, 74.25) * mm, "mid": v(-71.32, 71.32) * mm, "end": v(-74.25, 64.25) * mm});
            skLineSegment(sketch, "E93.1", {"start": v(-74.25, -64.25) * mm, "end": v(-74.25, 64.25) * mm});
            skArc(sketch, "E93.2", {"start": v(-74.25, -64.25) * mm, "mid": v(-71.32, -71.32) * mm, "end": v(-64.25, -74.25) * mm});
            skLineSegment(sketch, "E93.3", {"start": v(-64.25, -74.25) * mm, "end": v(64.25, -74.25) * mm});
            skArc(sketch, "E93.4", {"start": v(64.25, -74.25) * mm, "mid": v(71.32, -71.32) * mm, "end": v(74.25, -64.25) * mm});
            skLineSegment(sketch, "E93.5", {"start": v(74.25, -64.25) * mm, "end": v(74.25, 64.25) * mm});
            skArc(sketch, "E93.6", {"start": v(74.25, 64.25) * mm, "mid": v(71.32, 71.32) * mm, "end": v(64.25, 74.25) * mm});
            skLineSegment(sketch, "E93.7", {"start": v(-64.25, 74.25) * mm, "end": v(64.25, 74.25) * mm});
            skArc(sketch, "E93.8", {"start": v(54.26, 47.88) * mm, "mid": v(0, 60) * mm, "end": v(-54.26, 47.88) * mm});
            skArc(sketch, "E93.9", {"start": v(-54.26, 47.88) * mm, "mid": v(-58.44, 44.2) * mm, "end": v(-60, 38.83) * mm});
            skLineSegment(sketch, "E93.10", {"start": v(-60, 38.83) * mm, "end": v(-60, -38.83) * mm});
            skArc(sketch, "E93.11", {"start": v(-60, -38.83) * mm, "mid": v(-58.44, -44.2) * mm, "end": v(-54.26, -47.88) * mm});
            skArc(sketch, "E93.12", {"start": v(-54.26, -47.88) * mm, "mid": v(0, -60) * mm, "end": v(54.26, -47.88) * mm});
            skArc(sketch, "E93.13", {"start": v(54.26, -47.88) * mm, "mid": v(58.44, -44.2) * mm, "end": v(60, -38.83) * mm});
            skLineSegment(sketch, "E93.14", {"start": v(60, 38.83) * mm, "end": v(60, -38.83) * mm});
            skArc(sketch, "E93.15", {"start": v(60, 38.83) * mm, "mid": v(58.44, 44.2) * mm, "end": v(54.26, 47.88) * mm});
            skCircle(sketch, "E93.16", {"center": v(-60, 60) * mm, "radius": 4 * mm});
            skCircle(sketch, "E93.17", {"center": v(-60, -60) * mm, "radius": 4 * mm});
            skCircle(sketch, "E93.18", {"center": v(60, -60) * mm, "radius": 4 * mm});
            skCircle(sketch, "E93.19", {"center": v(60, 60) * mm, "radius": 4 * mm});
            skSolve(sketch);
        }
        {
            var Q0;
            Q0 = qSketchRegion(id + "F16", true);
            extrude(context, id + "F17", {"entities" : qUnion([Q0]), "operationType" : NewBodyOperationType.ADD, "endBound" : BoundingType.SYMMETRIC, "depth" : 6 * mm});
        }
    });
